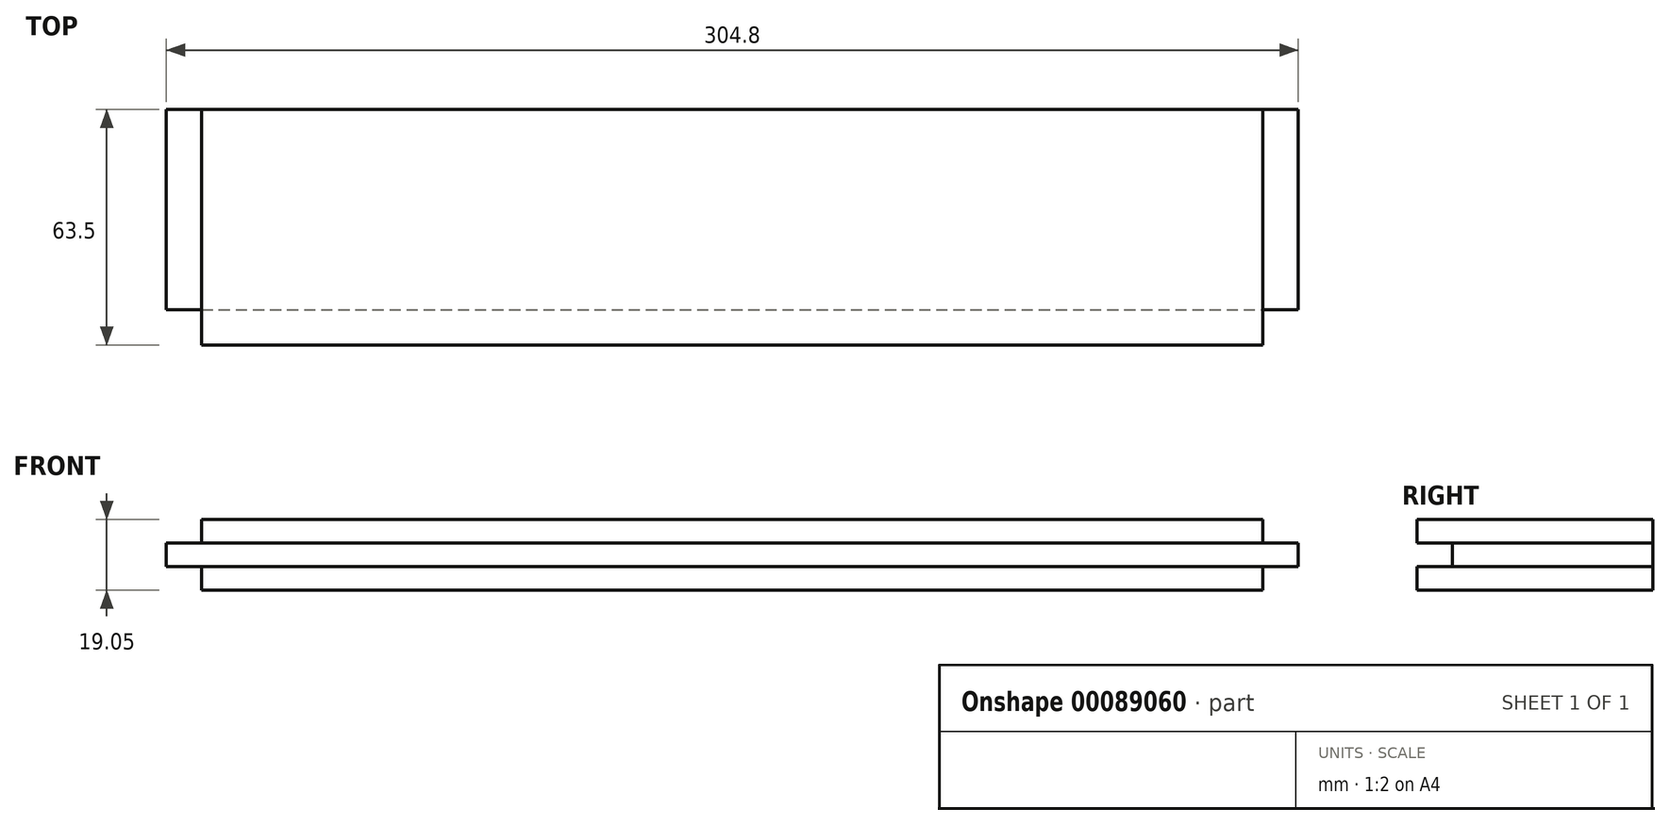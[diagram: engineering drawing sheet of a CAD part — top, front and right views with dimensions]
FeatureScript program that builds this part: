
annotation { "Feature Type Name" : "Feature", "Feature Type Description" : "" }
export const myFeature = defineFeature(function(context is Context, id is Id, definition is map)
    precondition{}
    {
        {
            var Q0;
            Q0=qCreatedBy(makeId("Right.planeOp"),FACE);
            var sketch = newSketch(context, id + "F0", { "sketchPlane" : qUnion([Q0])});
            skLineSegment(sketch, "E0.bottom", {"start": v(0, 0) * mm, "end": v(-63.5, 0) * mm});
            skLineSegment(sketch, "E0.top", {"start": v(0, 19.05) * mm, "end": v(-63.5, 19.05) * mm});
            skLineSegment(sketch, "E0.left", {"start": v(0, 0) * mm, "end": v(0, 19.05) * mm});
            skLineSegment(sketch, "E0.right", {"start": v(-63.5, 0) * mm, "end": v(-63.5, 19.05) * mm});
            skSolve(sketch);
        }
        {
            var Q0;
            Q0 = qSketchRegion(id + "F0", true);
            extrude(context, id + "F1", {"entities" : qUnion([Q0]), "endBound" : BoundingType.SYMMETRIC, "depth" : 304.8 * mm});
        }
        {
            var Q0;
            Q0=makeQuery(id+"F1.opExtrude","SWEPT_FACE",FACE,{"disambiguationData":[OSD([sQuery(id+"F0.wireOp",EDGE,"E0.right")])]});
            var sketch = newSketch(context, id + "F2", { "sketchPlane" : qUnion([Q0])});
            skLineSegment(sketch, "E1.bottom", {"start": v(152.4, 19.05) * mm, "end": v(142.88, 19.05) * mm});
            skLineSegment(sketch, "E1.top", {"start": v(152.4, 12.7) * mm, "end": v(142.88, 12.7) * mm});
            skLineSegment(sketch, "E1.left", {"start": v(152.4, 19.05) * mm, "end": v(152.4, 12.7) * mm});
            skLineSegment(sketch, "E1.right", {"start": v(142.88, 19.05) * mm, "end": v(142.88, 12.7) * mm});
            skLineSegment(sketch, "E2.bottom", {"start": v(152.4, 0) * mm, "end": v(142.88, 0) * mm});
            skLineSegment(sketch, "E2.top", {"start": v(152.4, 6.35) * mm, "end": v(142.88, 6.35) * mm});
            skLineSegment(sketch, "E2.left", {"start": v(152.4, 0) * mm, "end": v(152.4, 6.35) * mm});
            skLineSegment(sketch, "E2.right", {"start": v(142.88, 0) * mm, "end": v(142.88, 6.35) * mm});
            skLineSegment(sketch, "E3.bottom", {"start": v(-152.4, 19.05) * mm, "end": v(-142.88, 19.05) * mm});
            skLineSegment(sketch, "E3.top", {"start": v(-152.4, 12.7) * mm, "end": v(-142.88, 12.7) * mm});
            skLineSegment(sketch, "E3.left", {"start": v(-152.4, 19.05) * mm, "end": v(-152.4, 12.7) * mm});
            skLineSegment(sketch, "E3.right", {"start": v(-142.88, 19.05) * mm, "end": v(-142.88, 12.7) * mm});
            skLineSegment(sketch, "E4.bottom", {"start": v(-152.4, 0) * mm, "end": v(-142.88, 0) * mm});
            skLineSegment(sketch, "E4.top", {"start": v(-152.4, 6.35) * mm, "end": v(-142.88, 6.35) * mm});
            skLineSegment(sketch, "E4.left", {"start": v(-152.4, 0) * mm, "end": v(-152.4, 6.35) * mm});
            skLineSegment(sketch, "E4.right", {"start": v(-142.88, 0) * mm, "end": v(-142.88, 6.35) * mm});
            skSolve(sketch);
        }
        {
            var Q0;
            Q0 = qSketchRegion(id + "F2", true);
            extrude(context, id + "F3", {"entities" : qUnion([Q0]), "operationType" : NewBodyOperationType.REMOVE, "endBound" : BoundingType.THROUGH_ALL, "oppositeDirection" : true, "depth" : 25.4 * mm});
        }
        {
            var Q0;
            Q0=makeQuery(id+"F1.opExtrude","CAP_FACE",FACE,{"disambiguationData":[OSD([sQuery(id+"F0.wireOp",EDGE,"E0.bottom"),sQuery(id+"F0.wireOp",EDGE,"E0.top"),sQuery(id+"F0.wireOp",EDGE,"E0.left"),sQuery(id+"F0.wireOp",EDGE,"E0.right")])],"isStart":false});
            var sketch = newSketch(context, id + "F4", { "sketchPlane" : qUnion([Q0])});
            skLineSegment(sketch, "E5.bottom", {"start": v(-63.5, 12.7) * mm, "end": v(-53.98, 12.7) * mm});
            skLineSegment(sketch, "E5.top", {"start": v(-63.5, 6.35) * mm, "end": v(-53.98, 6.35) * mm});
            skLineSegment(sketch, "E5.left", {"start": v(-63.5, 12.7) * mm, "end": v(-63.5, 6.35) * mm});
            skLineSegment(sketch, "E5.right", {"start": v(-53.98, 12.7) * mm, "end": v(-53.98, 6.35) * mm});
            skSolve(sketch);
        }
        {
            var Q0;
            Q0 = qSketchRegion(id + "F4", true);
            extrude(context, id + "F5", {"entities" : qUnion([Q0]), "operationType" : NewBodyOperationType.REMOVE, "endBound" : BoundingType.THROUGH_ALL, "oppositeDirection" : true, "depth" : 25.4 * mm});
        }
    });
